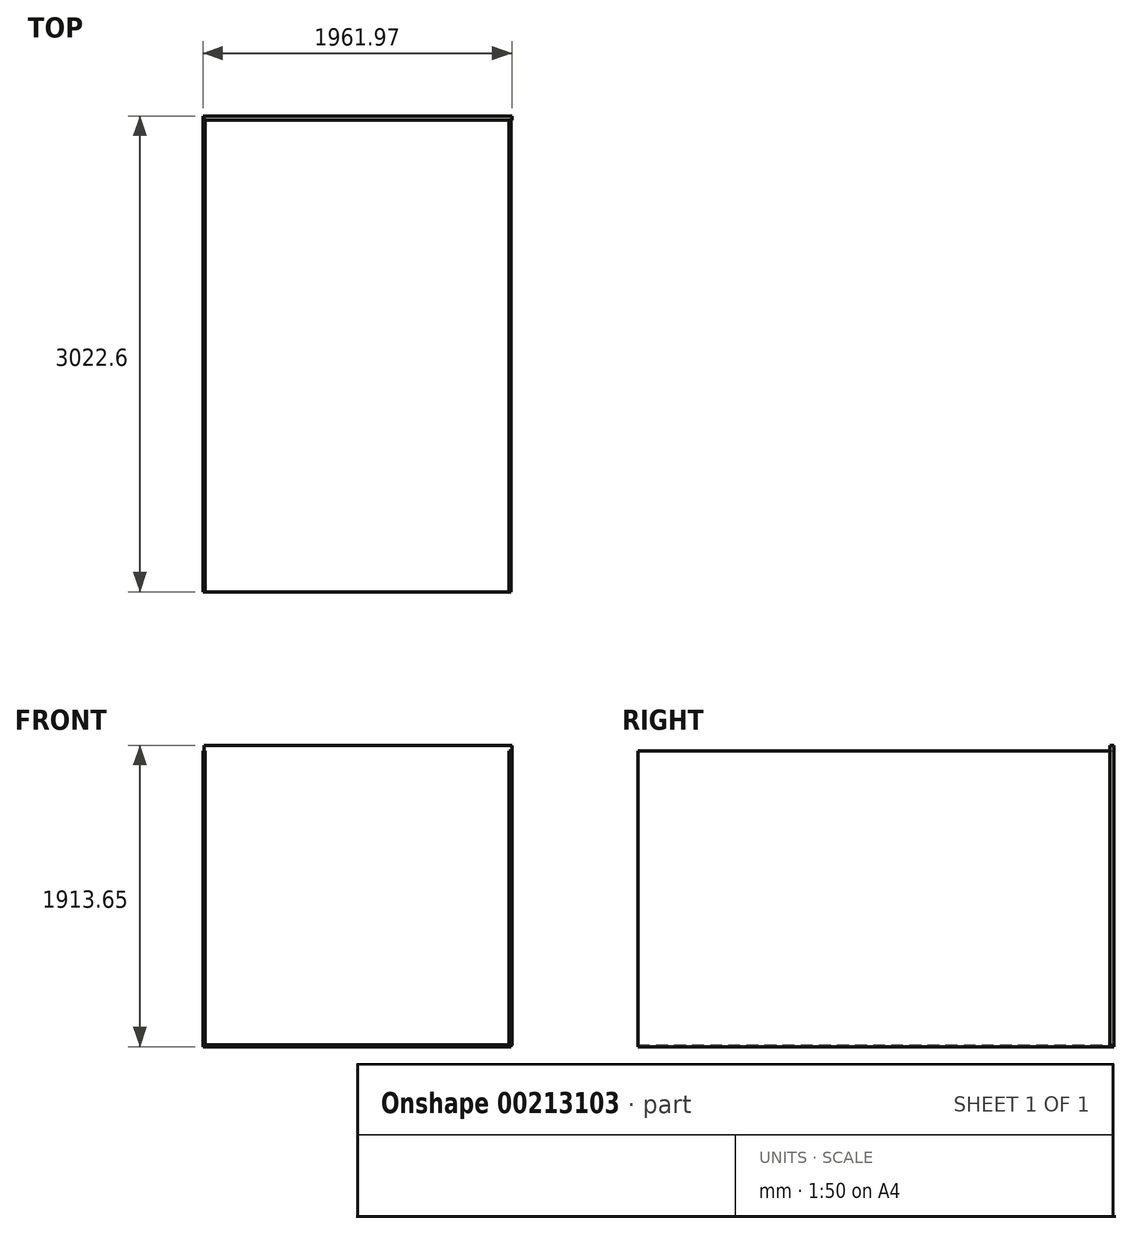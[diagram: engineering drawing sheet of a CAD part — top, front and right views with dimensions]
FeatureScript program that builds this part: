
annotation { "Feature Type Name" : "Feature", "Feature Type Description" : "" }
export const myFeature = defineFeature(function(context is Context, id is Id, definition is map)
    precondition{}
    {
        {
            var Q0;
            Q0=qCreatedBy(makeId("Front.planeOp"),FACE);
            var sketch = newSketch(context, id + "F0", { "sketchPlane" : qUnion([Q0])});
            skLineSegment(sketch, "E0.bottom", {"start": v(-48.43, 1863.28) * mm, "end": v(1907.37, 1863.28) * mm});
            skLineSegment(sketch, "E0.top", {"start": v(-48.43, -41.72) * mm, "end": v(1907.37, -41.72) * mm});
            skLineSegment(sketch, "E0.left", {"start": v(-48.43, 1863.28) * mm, "end": v(-48.43, -41.72) * mm});
            skLineSegment(sketch, "E0.right", {"start": v(1907.37, 1863.28) * mm, "end": v(1907.37, -41.72) * mm});
            skLineSegment(sketch, "E1.bottom", {"start": v(1894.67, 1850.58) * mm, "end": v(-35.73, 1850.58) * mm});
            skLineSegment(sketch, "E1.top", {"start": v(1894.67, -29.02) * mm, "end": v(-35.73, -29.02) * mm});
            skLineSegment(sketch, "E1.left", {"start": v(1894.67, 1850.58) * mm, "end": v(1894.67, -29.02) * mm});
            skLineSegment(sketch, "E1.right", {"start": v(-35.73, 1850.58) * mm, "end": v(-35.73, -29.02) * mm});
            skSolve(sketch);
        }
        {
            var Q0;
            Q0=makeQuery(id+"F0.imprint","IMPRINT",FACE,{"disambiguationData":[TD([[makeQuery(id+"F0.imprint","IMPRINT",EDGE,{"derivedFrom":sQuery(id+"F0.wireOp",EDGE,"E0.bottom")}),-1.0]])]});
            extrude(context, id + "F1", {"entities" : qUnion([Q0]), "depth" : 3022.6 * mm});
        }
        {
            var Q0;
            Q0=qCreatedBy(makeId("Front.planeOp"),FACE);
            var sketch = newSketch(context, id + "F2", { "sketchPlane" : qUnion([Q0])});
            skLineSegment(sketch, "E2.bottom", {"start": v(1913.54, 1871.93) * mm, "end": v(-42.26, 1871.93) * mm});
            skLineSegment(sketch, "E2.top", {"start": v(1913.54, -33.07) * mm, "end": v(-42.26, -33.07) * mm});
            skLineSegment(sketch, "E2.left", {"start": v(1913.54, 1871.93) * mm, "end": v(1913.54, -33.07) * mm});
            skLineSegment(sketch, "E2.right", {"start": v(-42.26, 1871.93) * mm, "end": v(-42.26, -33.07) * mm});
            skSolve(sketch);
        }
        {
            var Q0;
            Q0 = qSketchRegion(id + "F2", true);
            extrude(context, id + "F3", {"entities" : qUnion([Q0]), "operationType" : NewBodyOperationType.ADD, "depth" : 25.4 * mm});
        }
        {
            var Q0;
            Q0=makeQuery(id+"F1.opExtrude","SWEPT_FACE",FACE,{"disambiguationData":[OSD([sQuery(id+"F0.wireOp",EDGE,"E0.bottom")])]});
            extrude(context, id + "F4", {"entities" : qUnion([Q0]), "operationType" : NewBodyOperationType.REMOVE, "oppositeDirection" : true, "depth" : 25.4 * mm});
        }
    });
